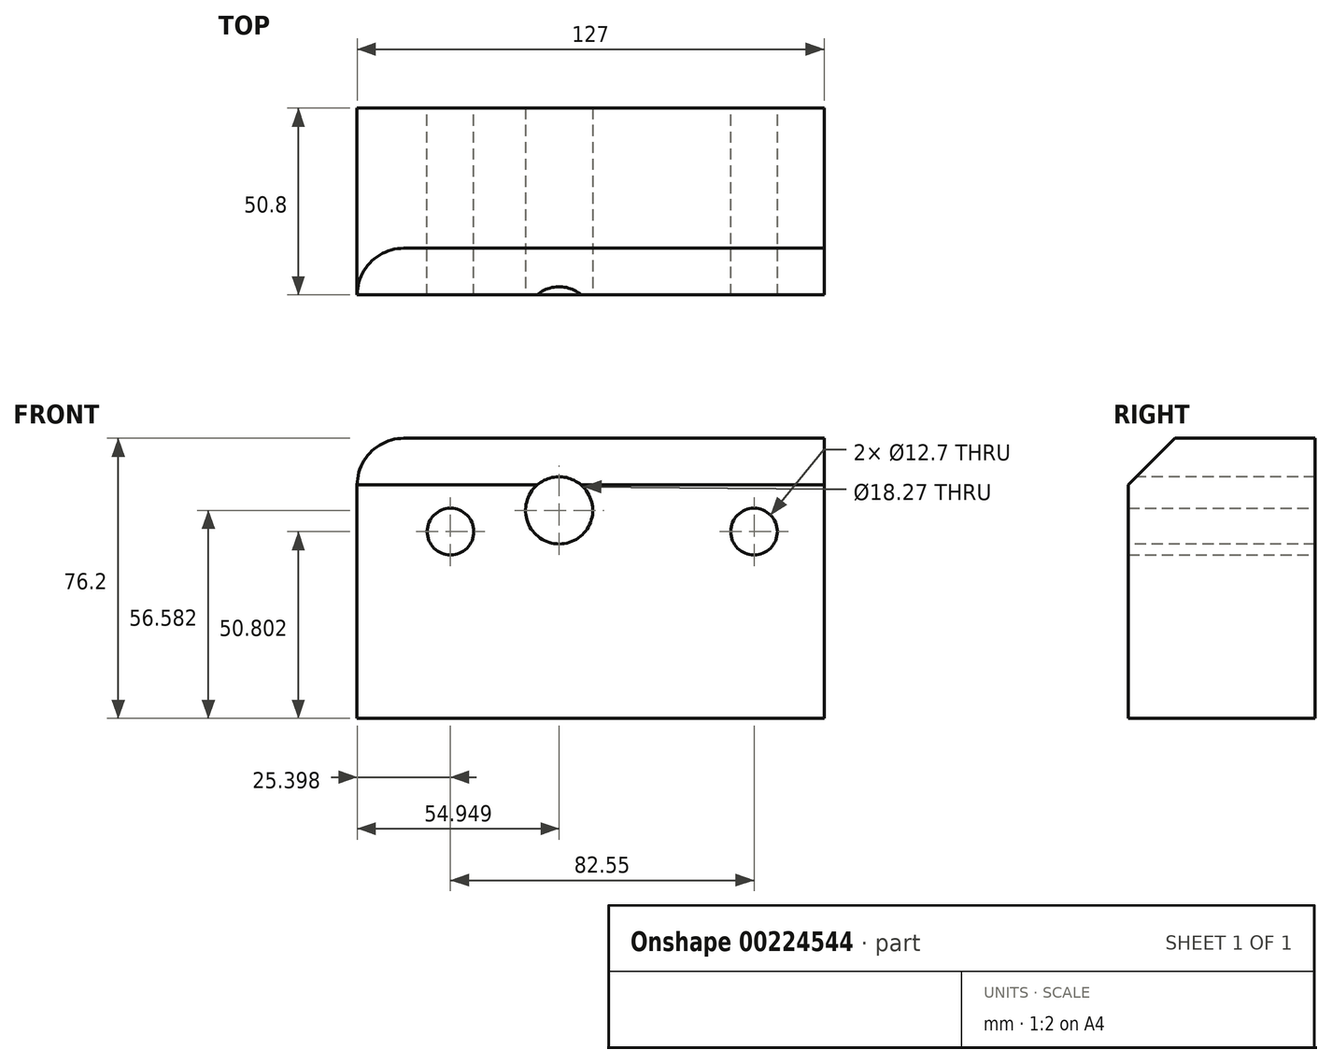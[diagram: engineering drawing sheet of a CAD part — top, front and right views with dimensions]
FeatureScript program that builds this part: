
annotation { "Feature Type Name" : "Feature", "Feature Type Description" : "" }
export const myFeature = defineFeature(function(context is Context, id is Id, definition is map)
    precondition{}
    {
        {
            var Q0;
            Q0=qCreatedBy(makeId("Front.planeOp"),FACE);
            var sketch = newSketch(context, id + "F0", { "sketchPlane" : qUnion([Q0])});
            skLineSegment(sketch, "E0.bottom", {"start": v(-58.52, -1.8) * mm, "end": v(68.48, -1.8) * mm});
            skLineSegment(sketch, "E0.top", {"start": v(-58.52, -78) * mm, "end": v(68.48, -78) * mm});
            skLineSegment(sketch, "E0.left", {"start": v(-58.52, -1.8) * mm, "end": v(-58.52, -78) * mm});
            skLineSegment(sketch, "E0.right", {"start": v(68.48, -1.8) * mm, "end": v(68.48, -78) * mm});
            skCircle(sketch, "E1", {"center": v(49.43, -27.2) * mm, "radius": 6.35 * mm});
            skCircle(sketch, "E2", {"center": v(-33.12, -27.2) * mm, "radius": 6.35 * mm});
            skSolve(sketch);
        }
        {
            var Q0;
            Q0=makeQuery(id+"F0.imprint","IMPRINT",FACE,{"disambiguationData":[TD([[makeQuery(id+"F0.imprint","IMPRINT",EDGE,{"derivedFrom":sQuery(id+"F0.wireOp",EDGE,"E0.bottom")}),-1.0]])]});
            extrude(context, id + "F1", {"entities" : qUnion([Q0]), "depth" : 50.8 * mm});
        }
        {
            var Q0;
            Q0=makeQuery(id+"F1.opExtrude","CAP_FACE",FACE,{"disambiguationData":[OSD([sQuery(id+"F0.wireOp",EDGE,"E0.bottom"),sQuery(id+"F0.wireOp",EDGE,"E0.top"),sQuery(id+"F0.wireOp",EDGE,"E0.left"),sQuery(id+"F0.wireOp",EDGE,"E0.right"),sQuery(id+"F0.wireOp",EDGE,"E1"),sQuery(id+"F0.wireOp",EDGE,"E2")])],"isStart":false});
            var sketch = newSketch(context, id + "F2", { "sketchPlane" : qUnion([Q0])});
            skCircle(sketch, "E3", {"center": v(-3.57, -21.42) * mm, "radius": 9.13 * mm});
            skSolve(sketch);
        }
        {
            var Q0;
            Q0=makeQuery(id+"F2.imprint","IMPRINT",FACE,{"disambiguationData":[TD([[makeQuery(id+"F2.imprint","IMPRINT",EDGE,{"derivedFrom":sQuery(id+"F2.wireOp",EDGE,"E3")}),1.0]])]});
            extrude(context, id + "F3", {"entities" : qUnion([Q0]), "operationType" : NewBodyOperationType.REMOVE, "oppositeDirection" : true, "depth" : 70.1 * mm});
        }
        {
            var Q0;
            Q0=makeQuery(id+"F1.opExtrude","CAP_EDGE",EDGE,{"disambiguationData":[OSD([sQuery(id+"F0.wireOp",EDGE,"E0.bottom")])],"isStart":false});
            chamfer(context, id + "F4", {"entities" : qUnion([Q0]), "width" : 12.7 * mm, "tangentPropagation" : true});
        }
        {
            var Q0;
            Q0=makeQuery(id+"F1.opExtrude","SWEPT_EDGE",EDGE,{"disambiguationData":[OSD([sQuery(id+"F0.wireOp",EDGE,"E0.bottom"),sQuery(id+"F0.wireOp",EDGE,"E0.left")])]});
            fillet(context, id + "F5", {"entities" : qUnion([Q0]), "radius" : 12.7 * mm, "tangentPropagation" : true, "allowEdgeOverflow" : false});
        }
    });
